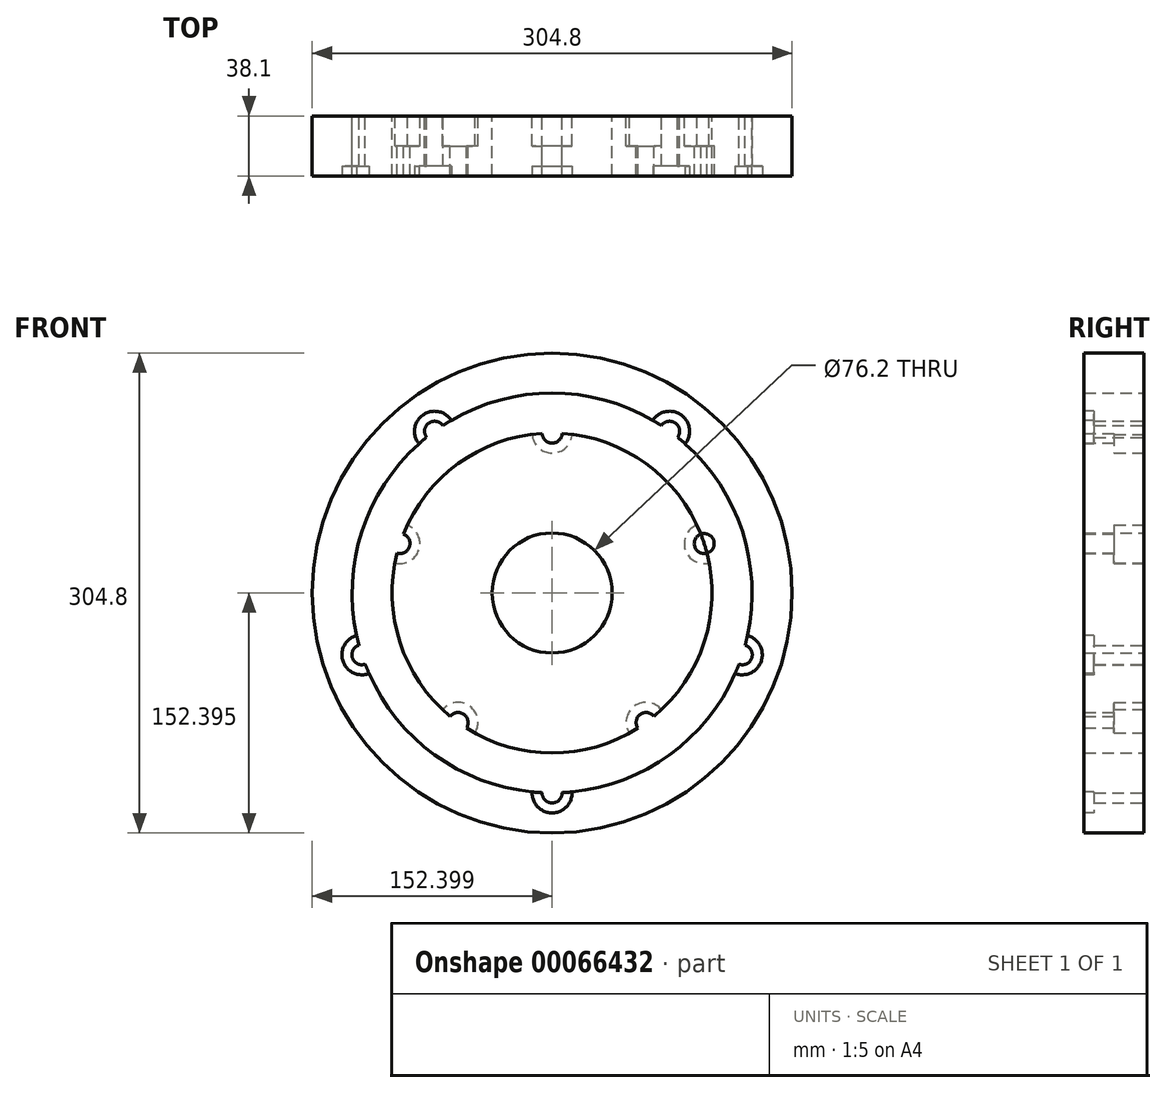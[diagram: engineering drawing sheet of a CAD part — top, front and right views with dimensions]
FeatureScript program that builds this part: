
annotation { "Feature Type Name" : "Feature", "Feature Type Description" : "" }
export const myFeature = defineFeature(function(context is Context, id is Id, definition is map)
    precondition{}
    {
        {
            var Q0;
            Q0=qCreatedBy(makeId("Front.planeOp"),FACE);
            var sketch = newSketch(context, id + "F0", { "sketchPlane" : qUnion([Q0])});
            skCircle(sketch, "E0", {"center": v(-14.28, 39.25) * mm, "radius": 152.4 * mm});
            skCircle(sketch, "E1", {"center": v(-14.28, 39.25) * mm, "radius": 38.1 * mm});
            skCircle(sketch, "E2", {"center": v(-14.28, 39.25) * mm, "radius": 101.6 * mm});
            skPoint(sketch, "E3", {"position": v(-14.28, 140.85) * mm});
            skPoint(sketch, "E4", {"position": v(-110.9, 70.64) * mm});
            skPoint(sketch, "E5", {"position": v(-74, -42.95) * mm});
            skPoint(sketch, "E6", {"position": v(45.44, -42.95) * mm});
            skPoint(sketch, "E7", {"position": v(82.35, 70.64) * mm});
            skCircle(sketch, "E8", {"center": v(-14.28, 39.25) * mm, "radius": 127 * mm});
            skPoint(sketch, "E9", {"position": v(-88.93, 142) * mm});
            skPoint(sketch, "E10", {"position": v(-135.06, 0) * mm});
            skPoint(sketch, "E11", {"position": v(-14.28, -87.75) * mm});
            skPoint(sketch, "E12", {"position": v(106.5, 0) * mm});
            skPoint(sketch, "E13", {"position": v(60.37, 142) * mm});
            skCircle(sketch, "E14", {"center": v(-14.28, 140.85) * mm, "radius": 6.35 * mm});
            skCircle(sketch, "E15", {"center": v(60.37, 142) * mm, "radius": 6.35 * mm});
            skCircle(sketch, "E16", {"center": v(82.35, 70.64) * mm, "radius": 6.35 * mm});
            skCircle(sketch, "E17", {"center": v(106.5, 0) * mm, "radius": 6.35 * mm});
            skCircle(sketch, "E18", {"center": v(45.44, -42.95) * mm, "radius": 6.35 * mm});
            skCircle(sketch, "E19", {"center": v(-14.28, -87.75) * mm, "radius": 6.35 * mm});
            skCircle(sketch, "E20", {"center": v(-74, -42.95) * mm, "radius": 6.35 * mm});
            skCircle(sketch, "E21", {"center": v(-135.06, 0) * mm, "radius": 6.35 * mm});
            skCircle(sketch, "E22", {"center": v(-110.9, 70.64) * mm, "radius": 6.35 * mm});
            skCircle(sketch, "E23", {"center": v(-88.93, 142) * mm, "radius": 6.35 * mm});
            skSolve(sketch);
        }
        {
            var Q0;
            Q0 = qSketchRegion(id + "F0", true);
            var Q1;
            {var subQ8=sQuery(id+"F0.wireOp",EDGE,"E16");var subQ9=sQuery(id+"F0.wireOp",EDGE,"E2");var subQ10=makeQuery(id+"F0.imprint","INTERSECT",VERTEX,{"disambiguationData":[OD(0.0)],"derivedFrom":[subQ9,subQ8]});Q1=makeQuery(id+"F0.imprint","IMPRINT",FACE,{"disambiguationData":[TD([[makeQuery(id+"F0.imprint","IMPRINT",EDGE,{"disambiguationData":[TD([[subQ10,-1.0]])],"derivedFrom":subQ9}),-1.0]])]});}
            var Q2;
            Q2=makeQuery(id+"F0.imprint","IMPRINT",FACE,{"disambiguationData":[TD([[makeQuery(id+"F0.imprint","IMPRINT",EDGE,{"derivedFrom":sQuery(id+"F0.wireOp",EDGE,"E1")}),-1.0]])]});
            extrude(context, id + "F1", {"entities" : qUnion([Q0, Q1, Q2]), "depth" : 38.1 * mm});
        }
        {
            var Q0;
            Q0=makeQuery(id+"F1.opExtrude","CAP_FACE",FACE,{"disambiguationData":[OSD([sQuery(id+"F0.wireOp",EDGE,"E0"),sQuery(id+"F0.wireOp",EDGE,"E1"),sQuery(id+"F0.wireOp",EDGE,"E14"),sQuery(id+"F0.wireOp",EDGE,"E15"),sQuery(id+"F0.wireOp",EDGE,"E16"),sQuery(id+"F0.wireOp",EDGE,"E17"),sQuery(id+"F0.wireOp",EDGE,"E18"),sQuery(id+"F0.wireOp",EDGE,"E19"),sQuery(id+"F0.wireOp",EDGE,"E20"),sQuery(id+"F0.wireOp",EDGE,"E21"),sQuery(id+"F0.wireOp",EDGE,"E22"),sQuery(id+"F0.wireOp",EDGE,"E23")])],"isStart":true});
            var sketch = newSketch(context, id + "F2", { "sketchPlane" : qUnion([Q0])});
            skCircle(sketch, "E24", {"center": v(14.28, 140.85) * mm, "radius": 12.7 * mm});
            skCircle(sketch, "E25", {"center": v(-82.35, 70.64) * mm, "radius": 12.7 * mm});
            skCircle(sketch, "E26", {"center": v(-45.44, -42.95) * mm, "radius": 12.7 * mm});
            skCircle(sketch, "E27", {"center": v(74, -42.95) * mm, "radius": 12.7 * mm});
            skCircle(sketch, "E28", {"center": v(110.9, 70.64) * mm, "radius": 12.7 * mm});
            skSolve(sketch);
        }
        {
            var Q0;
            Q0 = qSketchRegion(id + "F2", true);
            extrude(context, id + "F3", {"entities" : qUnion([Q0]), "operationType" : NewBodyOperationType.REMOVE, "oppositeDirection" : true, "depth" : 19.05 * mm});
        }
        {
            var Q0;
            Q0=makeQuery(id+"F1.opExtrude","CAP_FACE",FACE,{"disambiguationData":[OSD([sQuery(id+"F0.wireOp",EDGE,"E0"),sQuery(id+"F0.wireOp",EDGE,"E1"),sQuery(id+"F0.wireOp",EDGE,"E14"),sQuery(id+"F0.wireOp",EDGE,"E15"),sQuery(id+"F0.wireOp",EDGE,"E16"),sQuery(id+"F0.wireOp",EDGE,"E17"),sQuery(id+"F0.wireOp",EDGE,"E18"),sQuery(id+"F0.wireOp",EDGE,"E19"),sQuery(id+"F0.wireOp",EDGE,"E20"),sQuery(id+"F0.wireOp",EDGE,"E21"),sQuery(id+"F0.wireOp",EDGE,"E22"),sQuery(id+"F0.wireOp",EDGE,"E23")])],"isStart":false});
            var sketch = newSketch(context, id + "F4", { "sketchPlane" : qUnion([Q0])});
            skCircle(sketch, "E29", {"center": v(-88.93, 142) * mm, "radius": 12.7 * mm});
            skCircle(sketch, "E30", {"center": v(-135.06, 0) * mm, "radius": 12.7 * mm});
            skCircle(sketch, "E31", {"center": v(-14.28, -87.75) * mm, "radius": 12.7 * mm});
            skCircle(sketch, "E32", {"center": v(106.5, 0) * mm, "radius": 12.7 * mm});
            skCircle(sketch, "E33", {"center": v(60.37, 142) * mm, "radius": 12.7 * mm});
            skSolve(sketch);
        }
        {
            var Q0;
            Q0 = qSketchRegion(id + "F4", true);
            extrude(context, id + "F5", {"entities" : qUnion([Q0]), "operationType" : NewBodyOperationType.REMOVE, "oppositeDirection" : true, "depth" : 6.35 * mm});
        }
    });
